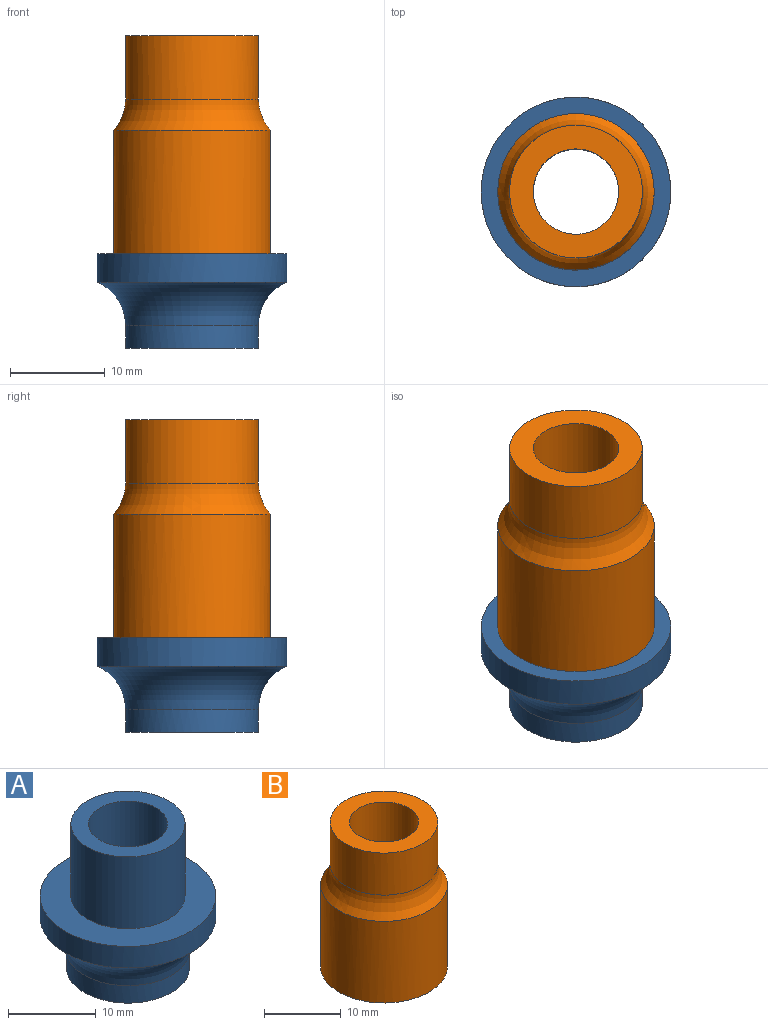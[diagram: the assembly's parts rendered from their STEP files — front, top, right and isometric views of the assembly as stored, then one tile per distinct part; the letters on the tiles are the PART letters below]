
ASSEMBLY  parts=2 mates=1
PART A: 8 faces, bbox 26x26x21.1 mm
  f0: cylinder r=4.5mm len=20mm, axis (0,0,-1), area 565.5mm2, adj f2,f6
  f1: cylinder r=6.5mm len=13mm, axis (0,0,-1), area 408.4mm2, adj f2,f4
  f2: plane 13x13mm, normal (0,0,1), area 69.1mm2, adj f0,f1
  f3: cylinder r=10mm len=20mm, axis (0,0,1), area 188.5mm2, adj f4,f7
  f4: plane 20x20mm, normal (0,0,1), area 181.4mm2, adj f1,f3
  f5: cylinder r=7mm len=14mm, axis (0,0,1), area 106.3mm2, adj f6,f7
  f6: plane 14x14mm, normal (0,0,-1), area 90.3mm2, adj f0,f5
  f7: torus R=12mm, axis (0,0,1), area 293.1mm2, adj f3,f5
PART B: 8 faces, bbox 18.3x18.3x23 mm
  f0: cylinder r=6.75mm len=13.5mm, axis (0,0,-1), area 424.1mm2, adj f2,f3
  f1: cylinder r=8.25mm len=16.5mm, axis (0,0,-1), area 673.9mm2, adj f2,f7
  f2: plane 16.5x16.5mm, normal (0,0,-1), area 70.7mm2, adj f0,f1
  f3: plane 13.5x13.5mm, normal (0,0,-1), area 79.5mm2, adj f0,f4
  f4: cylinder r=4.5mm len=13mm, axis (0,0,-1), area 367.6mm2, adj f3,f6
  f5: cylinder r=7mm len=14mm, axis (0,0,-1), area 294.4mm2, adj f6,f7
  f6: plane 14x14mm, normal (0,0,1), area 90.3mm2, adj f4,f5
  f7: torus R=12mm, axis (0,0,-1), area 168.6mm2, adj f1,f5
PLACE A t=(4.9,-25.88,43.59)mm
PLACE B t=(4.9,-25.88,43.59)mm
MATE fastened A.f1 <-> B.f0  axis (0,0,1) through (4.9,-25.88,53.59)mm
